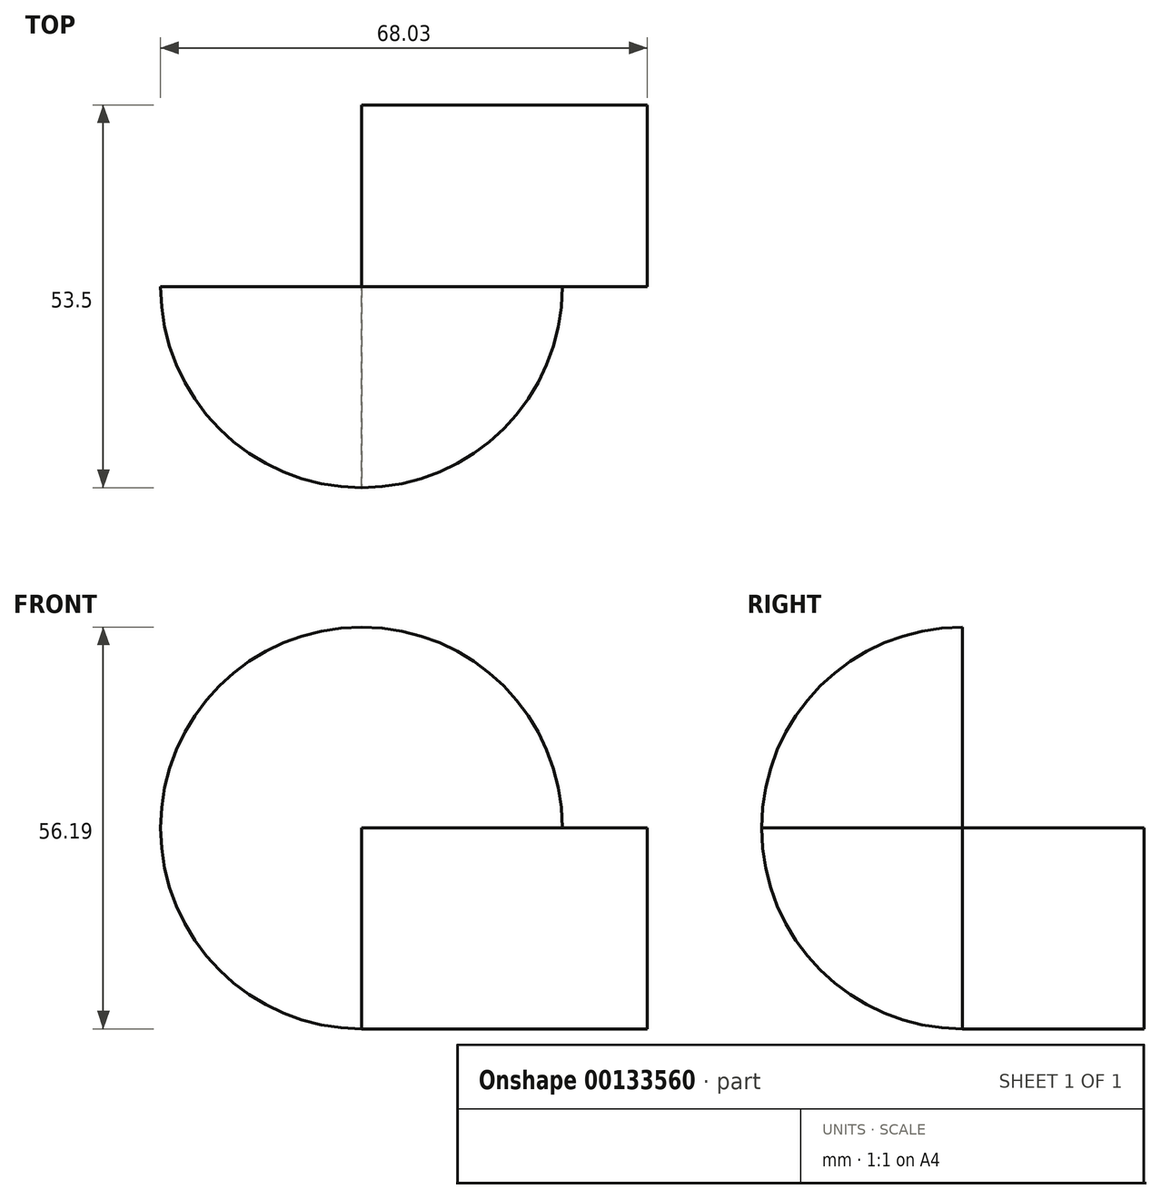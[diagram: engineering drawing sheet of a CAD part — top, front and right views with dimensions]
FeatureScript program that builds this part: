
annotation { "Feature Type Name" : "Feature", "Feature Type Description" : "" }
export const myFeature = defineFeature(function(context is Context, id is Id, definition is map)
    precondition{}
    {
        {
            var Q0;
            Q0=qCreatedBy(makeId("Front.planeOp"),FACE);
            var sketch = newSketch(context, id + "F0", { "sketchPlane" : qUnion([Q0])});
            skLineSegment(sketch, "E0.bottom", {"start": v(-39.93, 28.1) * mm, "end": v(0, 28.1) * mm});
            skLineSegment(sketch, "E0.top", {"start": v(-39.93, 0) * mm, "end": v(0, 0) * mm});
            skLineSegment(sketch, "E0.left", {"start": v(-39.93, 28.1) * mm, "end": v(-39.93, 0) * mm});
            skLineSegment(sketch, "E0.right", {"start": v(0, 28.1) * mm, "end": v(0, 0) * mm});
            skSolve(sketch);
        }
        {
            var Q0;
            Q0=makeQuery(id+"F0.imprint","IMPRINT",FACE,{"disambiguationData":[TD([[makeQuery(id+"F0.imprint","IMPRINT",EDGE,{"derivedFrom":sQuery(id+"F0.wireOp",EDGE,"E0.bottom")}),-1.0]])]});
            extrude(context, id + "F1", {"entities" : qUnion([Q0]), "depth" : 25.4 * mm});
        }
        {
            var Q0;
            Q0=makeQuery(id+"F0.imprint","IMPRINT",FACE,{"disambiguationData":[TD([[makeQuery(id+"F0.imprint","IMPRINT",EDGE,{"derivedFrom":sQuery(id+"F0.wireOp",EDGE,"E0.bottom")}),-1.0]])]});
            extrude(context, id + "F2", {"entities" : qUnion([Q0]), "depth" : 25.4 * mm});
        }
        {
            var Q0;
            Q0=makeQuery(id+"F1.opExtrude","CAP_FACE",FACE,{"disambiguationData":[OSD([sQuery(id+"F0.wireOp",EDGE,"E0.bottom"),sQuery(id+"F0.wireOp",EDGE,"E0.top"),sQuery(id+"F0.wireOp",EDGE,"E0.left"),sQuery(id+"F0.wireOp",EDGE,"E0.right")])],"isStart":false});
            var Q1;
            Q1=makeQuery(id+"F1.opExtrude","CAP_EDGE",EDGE,{"disambiguationData":[OSD([sQuery(id+"F0.wireOp",EDGE,"E0.bottom")])],"isStart":false});
            revolve(context, id + "F3", {"entities" : qUnion([Q0]), "axis" : qUnion([Q1]), "revolveType" : RevolveType.ONE_DIRECTION, "oppositeDirection" : true, "angle" : 90 * degree});
        }
        {
            var Q0;
            Q0=makeQuery(id+"F3.opRevolve","SWEPT_FACE",FACE,{"disambiguationData":[OSD([sQuery(id+"F0.wireOp",EDGE,"E0.left")])]});
            var Q1;
            Q1=makeQuery(id+"F3.opRevolve","CAP_EDGE",EDGE,{"disambiguationData":[OSD([sQuery(id+"F0.wireOp",EDGE,"E0.left")])],"isStart":false});
            revolve(context, id + "F4", {"entities" : qUnion([Q0]), "axis" : qUnion([Q1]), "revolveType" : RevolveType.FULL});
        }
        {
            var Q0;
            Q0=makeQuery(id+"F3.opRevolve","SWEPT_BODY",BODY,{"disambiguationData":[OSD([sQuery(id+"F0.wireOp",EDGE,"E0.bottom"),sQuery(id+"F0.wireOp",EDGE,"E0.top"),sQuery(id+"F0.wireOp",EDGE,"E0.left"),sQuery(id+"F0.wireOp",EDGE,"E0.right")])]});
            var Q1;
            Q1=makeQuery(id+"F4.opRevolve","SWEPT_BODY",BODY,{"disambiguationData":[OSD([sQuery(id+"F0.wireOp",EDGE,"E0.left")])]});
            booleanBodies(context, id + "F5", {"operationType" : BooleanOperationType.SUBTRACTION, "tools" : qUnion([Q0]), "targets" : qUnion([Q1])});
        }
    });
